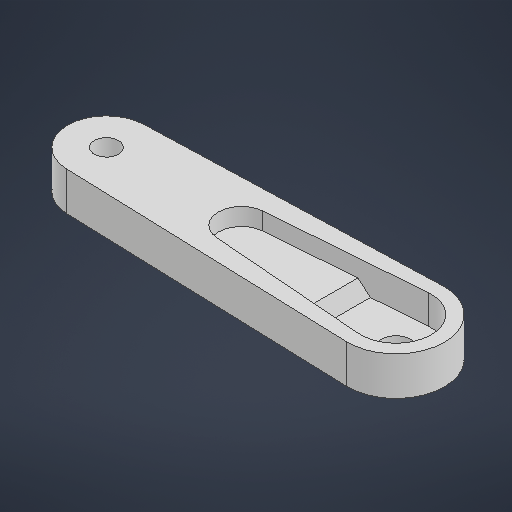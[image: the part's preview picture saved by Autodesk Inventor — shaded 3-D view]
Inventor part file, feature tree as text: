
AUTODESK INVENTOR PART (.ipt)
format: ipt  version: 2025.1 (Build 291241000, 241)  size: 468,992 bytes
history: native  units: mm
features: extrude x3, sketch x1, chamfer x1
ambient origin geometry x8: Origin, YZ Plane, XZ Plane, XY Plane, X Axis, Y Axis, Z Axis, Center Point
bodies: Solid1 (feature_tree)
feature tree (5):
  sketch  "Sketch1"  dims[d0=7.3mm d1=4.8mm d2=16.0mm d3=9.5mm d4=3.1mm d6=6.0mm d8=2.5mm d9=1.0mm d10=0.0mm d11=3.0mm d12=0.0mm d13=1.2mm d14=0.0mm d15=1.2mm d16=2.0mm d17=45.0deg d18=10.0mm d19=8.0mm d20=30.0mm]
  extrude  "Extrusion1"  Depth=30.0mm
  extrude  "Extrusion2"  Depth=1.0mm TaperAngle=0.0deg
  extrude  "Extrusion3"  Depth=3.0mm TaperAngle=0.0deg
  chamfer  "Chamfer1"  Distance=1.2mm
